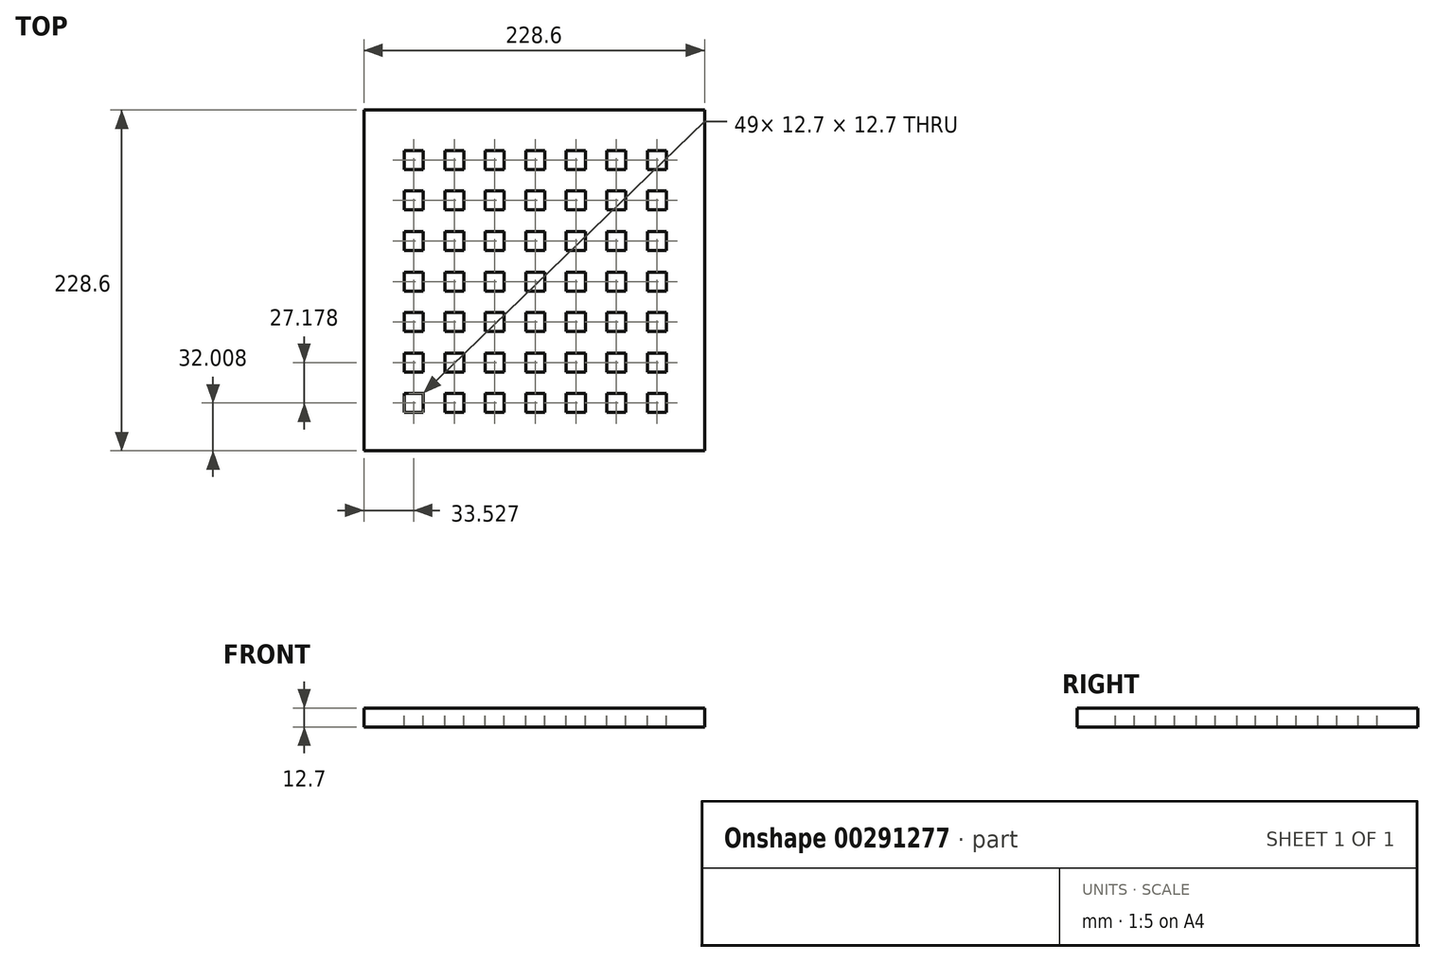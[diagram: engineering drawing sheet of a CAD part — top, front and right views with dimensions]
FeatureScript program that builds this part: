
annotation { "Feature Type Name" : "Feature", "Feature Type Description" : "" }
export const myFeature = defineFeature(function(context is Context, id is Id, definition is map)
    precondition{}
    {
        {
            var Q0;
            Q0=qCreatedBy(makeId("Top.planeOp"),FACE);
            var sketch = newSketch(context, id + "F0", { "sketchPlane" : qUnion([Q0])});
            skLineSegment(sketch, "E0.bottom", {"start": v(-111.6, 116.61) * mm, "end": v(117, 116.61) * mm});
            skLineSegment(sketch, "E0.top", {"start": v(-111.6, -111.99) * mm, "end": v(117, -111.99) * mm});
            skLineSegment(sketch, "E0.left", {"start": v(-111.6, 116.61) * mm, "end": v(-111.6, -111.99) * mm});
            skLineSegment(sketch, "E0.right", {"start": v(117, 116.61) * mm, "end": v(117, -111.99) * mm});
            skSolve(sketch);
        }
        {
            var Q0;
            Q0=makeQuery(id+"F0.imprint","IMPRINT",FACE,{"disambiguationData":[TD([[makeQuery(id+"F0.imprint","IMPRINT",EDGE,{"derivedFrom":sQuery(id+"F0.wireOp",EDGE,"E0.bottom")}),-1.0]])]});
            extrude(context, id + "F1", {"entities" : qUnion([Q0]), "depth" : 12.7 * mm});
        }
        {
            var Q0;
            Q0=makeQuery(id+"F1.opExtrude","CAP_FACE",FACE,{"disambiguationData":[OSD([sQuery(id+"F0.wireOp",EDGE,"E0.bottom"),sQuery(id+"F0.wireOp",EDGE,"E0.top"),sQuery(id+"F0.wireOp",EDGE,"E0.left"),sQuery(id+"F0.wireOp",EDGE,"E0.right")])],"isStart":false});
            var sketch = newSketch(context, id + "F2", { "sketchPlane" : qUnion([Q0])});
            skLineSegment(sketch, "E1.bottom", {"start": v(-111.6, 116.61) * mm, "end": v(-98.9, 116.61) * mm});
            skLineSegment(sketch, "E1.top", {"start": v(-111.6, 103.91) * mm, "end": v(-98.9, 103.91) * mm});
            skLineSegment(sketch, "E1.left", {"start": v(-111.6, 116.61) * mm, "end": v(-111.6, 103.91) * mm});
            skLineSegment(sketch, "E1.right", {"start": v(-98.9, 116.61) * mm, "end": v(-98.9, 103.91) * mm});
            skLineSegment(sketch, "E2.0.1.0", {"start": v(-98.9, 89.44) * mm, "end": v(-98.9, 76.74) * mm});
            skLineSegment(sketch, "E2.0.1.1", {"start": v(-111.6, 89.44) * mm, "end": v(-111.6, 76.74) * mm});
            skLineSegment(sketch, "E2.0.1.2", {"start": v(-111.6, 76.74) * mm, "end": v(-98.9, 76.74) * mm});
            skLineSegment(sketch, "E2.0.1.3", {"start": v(-111.6, 89.44) * mm, "end": v(-98.9, 89.44) * mm});
            skLineSegment(sketch, "E2.0.2.0", {"start": v(-98.9, 62.26) * mm, "end": v(-98.9, 49.56) * mm});
            skLineSegment(sketch, "E2.0.2.1", {"start": v(-111.6, 62.26) * mm, "end": v(-111.6, 49.56) * mm});
            skLineSegment(sketch, "E2.0.2.2", {"start": v(-111.6, 49.56) * mm, "end": v(-98.9, 49.56) * mm});
            skLineSegment(sketch, "E2.0.2.3", {"start": v(-111.6, 62.26) * mm, "end": v(-98.9, 62.26) * mm});
            skLineSegment(sketch, "E2.0.3.0", {"start": v(-98.9, 35.08) * mm, "end": v(-98.9, 22.38) * mm});
            skLineSegment(sketch, "E2.0.3.1", {"start": v(-111.6, 35.08) * mm, "end": v(-111.6, 22.38) * mm});
            skLineSegment(sketch, "E2.0.3.2", {"start": v(-111.6, 22.38) * mm, "end": v(-98.9, 22.38) * mm});
            skLineSegment(sketch, "E2.0.3.3", {"start": v(-111.6, 35.08) * mm, "end": v(-98.9, 35.08) * mm});
            skLineSegment(sketch, "E2.0.4.0", {"start": v(-98.9, 7.9) * mm, "end": v(-98.9, -4.8) * mm});
            skLineSegment(sketch, "E2.0.4.1", {"start": v(-111.6, 7.9) * mm, "end": v(-111.6, -4.8) * mm});
            skLineSegment(sketch, "E2.0.4.2", {"start": v(-111.6, -4.8) * mm, "end": v(-98.9, -4.8) * mm});
            skLineSegment(sketch, "E2.0.4.3", {"start": v(-111.6, 7.9) * mm, "end": v(-98.9, 7.9) * mm});
            skLineSegment(sketch, "E2.0.5.0", {"start": v(-98.9, -19.28) * mm, "end": v(-98.9, -31.98) * mm});
            skLineSegment(sketch, "E2.0.5.1", {"start": v(-111.6, -19.28) * mm, "end": v(-111.6, -31.98) * mm});
            skLineSegment(sketch, "E2.0.5.2", {"start": v(-111.6, -31.98) * mm, "end": v(-98.9, -31.98) * mm});
            skLineSegment(sketch, "E2.0.5.3", {"start": v(-111.6, -19.28) * mm, "end": v(-98.9, -19.28) * mm});
            skLineSegment(sketch, "E2.0.6.0", {"start": v(-98.9, -46.45) * mm, "end": v(-98.9, -59.15) * mm});
            skLineSegment(sketch, "E2.0.6.1", {"start": v(-111.6, -46.45) * mm, "end": v(-111.6, -59.15) * mm});
            skLineSegment(sketch, "E2.0.6.2", {"start": v(-111.6, -59.15) * mm, "end": v(-98.9, -59.15) * mm});
            skLineSegment(sketch, "E2.0.6.3", {"start": v(-111.6, -46.45) * mm, "end": v(-98.9, -46.45) * mm});
            skLineSegment(sketch, "E2.0.7.0", {"start": v(-98.9, -73.63) * mm, "end": v(-98.9, -86.33) * mm});
            skLineSegment(sketch, "E2.0.7.1", {"start": v(-111.6, -73.63) * mm, "end": v(-111.6, -86.33) * mm});
            skLineSegment(sketch, "E2.0.7.2", {"start": v(-111.6, -86.33) * mm, "end": v(-98.9, -86.33) * mm});
            skLineSegment(sketch, "E2.0.7.3", {"start": v(-111.6, -73.63) * mm, "end": v(-98.9, -73.63) * mm});
            skLineSegment(sketch, "E2.1.0.0", {"start": v(-71.71, 116.61) * mm, "end": v(-71.71, 103.91) * mm});
            skLineSegment(sketch, "E2.1.0.1", {"start": v(-84.41, 116.61) * mm, "end": v(-84.41, 103.91) * mm});
            skLineSegment(sketch, "E2.1.0.2", {"start": v(-84.41, 103.91) * mm, "end": v(-71.71, 103.91) * mm});
            skLineSegment(sketch, "E2.1.0.3", {"start": v(-84.41, 116.61) * mm, "end": v(-71.71, 116.61) * mm});
            skLineSegment(sketch, "E2.1.1.0", {"start": v(-71.71, 89.44) * mm, "end": v(-71.71, 76.74) * mm});
            skLineSegment(sketch, "E2.1.1.1", {"start": v(-84.41, 89.44) * mm, "end": v(-84.41, 76.74) * mm});
            skLineSegment(sketch, "E2.1.1.2", {"start": v(-84.41, 76.74) * mm, "end": v(-71.71, 76.74) * mm});
            skLineSegment(sketch, "E2.1.1.3", {"start": v(-84.41, 89.44) * mm, "end": v(-71.71, 89.44) * mm});
            skLineSegment(sketch, "E2.1.2.0", {"start": v(-71.71, 62.26) * mm, "end": v(-71.71, 49.56) * mm});
            skLineSegment(sketch, "E2.1.2.1", {"start": v(-84.41, 62.26) * mm, "end": v(-84.41, 49.56) * mm});
            skLineSegment(sketch, "E2.1.2.2", {"start": v(-84.41, 49.56) * mm, "end": v(-71.71, 49.56) * mm});
            skLineSegment(sketch, "E2.1.2.3", {"start": v(-84.41, 62.26) * mm, "end": v(-71.71, 62.26) * mm});
            skLineSegment(sketch, "E2.1.3.0", {"start": v(-71.71, 35.08) * mm, "end": v(-71.71, 22.38) * mm});
            skLineSegment(sketch, "E2.1.3.1", {"start": v(-84.41, 35.08) * mm, "end": v(-84.41, 22.38) * mm});
            skLineSegment(sketch, "E2.1.3.2", {"start": v(-84.41, 22.38) * mm, "end": v(-71.71, 22.38) * mm});
            skLineSegment(sketch, "E2.1.3.3", {"start": v(-84.41, 35.08) * mm, "end": v(-71.71, 35.08) * mm});
            skLineSegment(sketch, "E2.1.4.0", {"start": v(-71.71, 7.9) * mm, "end": v(-71.71, -4.8) * mm});
            skLineSegment(sketch, "E2.1.4.1", {"start": v(-84.41, 7.9) * mm, "end": v(-84.41, -4.8) * mm});
            skLineSegment(sketch, "E2.1.4.2", {"start": v(-84.41, -4.8) * mm, "end": v(-71.71, -4.8) * mm});
            skLineSegment(sketch, "E2.1.4.3", {"start": v(-84.41, 7.9) * mm, "end": v(-71.71, 7.9) * mm});
            skLineSegment(sketch, "E2.1.5.0", {"start": v(-71.71, -19.28) * mm, "end": v(-71.71, -31.98) * mm});
            skLineSegment(sketch, "E2.1.5.1", {"start": v(-84.41, -19.28) * mm, "end": v(-84.41, -31.98) * mm});
            skLineSegment(sketch, "E2.1.5.2", {"start": v(-84.41, -31.98) * mm, "end": v(-71.71, -31.98) * mm});
            skLineSegment(sketch, "E2.1.5.3", {"start": v(-84.41, -19.28) * mm, "end": v(-71.71, -19.28) * mm});
            skLineSegment(sketch, "E2.1.6.0", {"start": v(-71.71, -46.45) * mm, "end": v(-71.71, -59.15) * mm});
            skLineSegment(sketch, "E2.1.6.1", {"start": v(-84.41, -46.45) * mm, "end": v(-84.41, -59.15) * mm});
            skLineSegment(sketch, "E2.1.6.2", {"start": v(-84.41, -59.15) * mm, "end": v(-71.71, -59.15) * mm});
            skLineSegment(sketch, "E2.1.6.3", {"start": v(-84.41, -46.45) * mm, "end": v(-71.71, -46.45) * mm});
            skLineSegment(sketch, "E2.1.7.0", {"start": v(-71.71, -73.63) * mm, "end": v(-71.71, -86.33) * mm});
            skLineSegment(sketch, "E2.1.7.1", {"start": v(-84.41, -73.63) * mm, "end": v(-84.41, -86.33) * mm});
            skLineSegment(sketch, "E2.1.7.2", {"start": v(-84.41, -86.33) * mm, "end": v(-71.71, -86.33) * mm});
            skLineSegment(sketch, "E2.1.7.3", {"start": v(-84.41, -73.63) * mm, "end": v(-71.71, -73.63) * mm});
            skLineSegment(sketch, "E2.2.0.0", {"start": v(-44.53, 116.61) * mm, "end": v(-44.53, 103.91) * mm});
            skLineSegment(sketch, "E2.2.0.1", {"start": v(-57.23, 116.61) * mm, "end": v(-57.23, 103.91) * mm});
            skLineSegment(sketch, "E2.2.0.2", {"start": v(-57.23, 103.91) * mm, "end": v(-44.53, 103.91) * mm});
            skLineSegment(sketch, "E2.2.0.3", {"start": v(-57.23, 116.61) * mm, "end": v(-44.53, 116.61) * mm});
            skLineSegment(sketch, "E2.2.1.0", {"start": v(-44.53, 89.44) * mm, "end": v(-44.53, 76.74) * mm});
            skLineSegment(sketch, "E2.2.1.1", {"start": v(-57.23, 89.44) * mm, "end": v(-57.23, 76.74) * mm});
            skLineSegment(sketch, "E2.2.1.2", {"start": v(-57.23, 76.74) * mm, "end": v(-44.53, 76.74) * mm});
            skLineSegment(sketch, "E2.2.1.3", {"start": v(-57.23, 89.44) * mm, "end": v(-44.53, 89.44) * mm});
            skLineSegment(sketch, "E2.2.2.0", {"start": v(-44.53, 62.26) * mm, "end": v(-44.53, 49.56) * mm});
            skLineSegment(sketch, "E2.2.2.1", {"start": v(-57.23, 62.26) * mm, "end": v(-57.23, 49.56) * mm});
            skLineSegment(sketch, "E2.2.2.2", {"start": v(-57.23, 49.56) * mm, "end": v(-44.53, 49.56) * mm});
            skLineSegment(sketch, "E2.2.2.3", {"start": v(-57.23, 62.26) * mm, "end": v(-44.53, 62.26) * mm});
            skLineSegment(sketch, "E2.2.3.0", {"start": v(-44.53, 35.08) * mm, "end": v(-44.53, 22.38) * mm});
            skLineSegment(sketch, "E2.2.3.1", {"start": v(-57.23, 35.08) * mm, "end": v(-57.23, 22.38) * mm});
            skLineSegment(sketch, "E2.2.3.2", {"start": v(-57.23, 22.38) * mm, "end": v(-44.53, 22.38) * mm});
            skLineSegment(sketch, "E2.2.3.3", {"start": v(-57.23, 35.08) * mm, "end": v(-44.53, 35.08) * mm});
            skLineSegment(sketch, "E2.2.4.0", {"start": v(-44.53, 7.9) * mm, "end": v(-44.53, -4.8) * mm});
            skLineSegment(sketch, "E2.2.4.1", {"start": v(-57.23, 7.9) * mm, "end": v(-57.23, -4.8) * mm});
            skLineSegment(sketch, "E2.2.4.2", {"start": v(-57.23, -4.8) * mm, "end": v(-44.53, -4.8) * mm});
            skLineSegment(sketch, "E2.2.4.3", {"start": v(-57.23, 7.9) * mm, "end": v(-44.53, 7.9) * mm});
            skLineSegment(sketch, "E2.2.5.0", {"start": v(-44.53, -19.28) * mm, "end": v(-44.53, -31.98) * mm});
            skLineSegment(sketch, "E2.2.5.1", {"start": v(-57.23, -19.28) * mm, "end": v(-57.23, -31.98) * mm});
            skLineSegment(sketch, "E2.2.5.2", {"start": v(-57.23, -31.98) * mm, "end": v(-44.53, -31.98) * mm});
            skLineSegment(sketch, "E2.2.5.3", {"start": v(-57.23, -19.28) * mm, "end": v(-44.53, -19.28) * mm});
            skLineSegment(sketch, "E2.2.6.0", {"start": v(-44.53, -46.45) * mm, "end": v(-44.53, -59.15) * mm});
            skLineSegment(sketch, "E2.2.6.1", {"start": v(-57.23, -46.45) * mm, "end": v(-57.23, -59.15) * mm});
            skLineSegment(sketch, "E2.2.6.2", {"start": v(-57.23, -59.15) * mm, "end": v(-44.53, -59.15) * mm});
            skLineSegment(sketch, "E2.2.6.3", {"start": v(-57.23, -46.45) * mm, "end": v(-44.53, -46.45) * mm});
            skLineSegment(sketch, "E2.2.7.0", {"start": v(-44.53, -73.63) * mm, "end": v(-44.53, -86.33) * mm});
            skLineSegment(sketch, "E2.2.7.1", {"start": v(-57.23, -73.63) * mm, "end": v(-57.23, -86.33) * mm});
            skLineSegment(sketch, "E2.2.7.2", {"start": v(-57.23, -86.33) * mm, "end": v(-44.53, -86.33) * mm});
            skLineSegment(sketch, "E2.2.7.3", {"start": v(-57.23, -73.63) * mm, "end": v(-44.53, -73.63) * mm});
            skLineSegment(sketch, "E2.3.0.0", {"start": v(-17.36, 116.61) * mm, "end": v(-17.36, 103.91) * mm});
            skLineSegment(sketch, "E2.3.0.1", {"start": v(-30.06, 116.61) * mm, "end": v(-30.06, 103.91) * mm});
            skLineSegment(sketch, "E2.3.0.2", {"start": v(-30.06, 103.91) * mm, "end": v(-17.36, 103.91) * mm});
            skLineSegment(sketch, "E2.3.0.3", {"start": v(-30.06, 116.61) * mm, "end": v(-17.36, 116.61) * mm});
            skLineSegment(sketch, "E2.3.1.0", {"start": v(-17.36, 89.44) * mm, "end": v(-17.36, 76.74) * mm});
            skLineSegment(sketch, "E2.3.1.1", {"start": v(-30.06, 89.44) * mm, "end": v(-30.06, 76.74) * mm});
            skLineSegment(sketch, "E2.3.1.2", {"start": v(-30.06, 76.74) * mm, "end": v(-17.36, 76.74) * mm});
            skLineSegment(sketch, "E2.3.1.3", {"start": v(-30.06, 89.44) * mm, "end": v(-17.36, 89.44) * mm});
            skLineSegment(sketch, "E2.3.2.0", {"start": v(-17.36, 62.26) * mm, "end": v(-17.36, 49.56) * mm});
            skLineSegment(sketch, "E2.3.2.1", {"start": v(-30.06, 62.26) * mm, "end": v(-30.06, 49.56) * mm});
            skLineSegment(sketch, "E2.3.2.2", {"start": v(-30.06, 49.56) * mm, "end": v(-17.36, 49.56) * mm});
            skLineSegment(sketch, "E2.3.2.3", {"start": v(-30.06, 62.26) * mm, "end": v(-17.36, 62.26) * mm});
            skLineSegment(sketch, "E2.3.3.0", {"start": v(-17.36, 35.08) * mm, "end": v(-17.36, 22.38) * mm});
            skLineSegment(sketch, "E2.3.3.1", {"start": v(-30.06, 35.08) * mm, "end": v(-30.06, 22.38) * mm});
            skLineSegment(sketch, "E2.3.3.2", {"start": v(-30.06, 22.38) * mm, "end": v(-17.36, 22.38) * mm});
            skLineSegment(sketch, "E2.3.3.3", {"start": v(-30.06, 35.08) * mm, "end": v(-17.36, 35.08) * mm});
            skLineSegment(sketch, "E2.3.4.0", {"start": v(-17.36, 7.9) * mm, "end": v(-17.36, -4.8) * mm});
            skLineSegment(sketch, "E2.3.4.1", {"start": v(-30.06, 7.9) * mm, "end": v(-30.06, -4.8) * mm});
            skLineSegment(sketch, "E2.3.4.2", {"start": v(-30.06, -4.8) * mm, "end": v(-17.36, -4.8) * mm});
            skLineSegment(sketch, "E2.3.4.3", {"start": v(-30.06, 7.9) * mm, "end": v(-17.36, 7.9) * mm});
            skLineSegment(sketch, "E2.3.5.0", {"start": v(-17.36, -19.28) * mm, "end": v(-17.36, -31.98) * mm});
            skLineSegment(sketch, "E2.3.5.1", {"start": v(-30.06, -19.28) * mm, "end": v(-30.06, -31.98) * mm});
            skLineSegment(sketch, "E2.3.5.2", {"start": v(-30.06, -31.98) * mm, "end": v(-17.36, -31.98) * mm});
            skLineSegment(sketch, "E2.3.5.3", {"start": v(-30.06, -19.28) * mm, "end": v(-17.36, -19.28) * mm});
            skLineSegment(sketch, "E2.3.6.0", {"start": v(-17.36, -46.45) * mm, "end": v(-17.36, -59.15) * mm});
            skLineSegment(sketch, "E2.3.6.1", {"start": v(-30.06, -46.45) * mm, "end": v(-30.06, -59.15) * mm});
            skLineSegment(sketch, "E2.3.6.2", {"start": v(-30.06, -59.15) * mm, "end": v(-17.36, -59.15) * mm});
            skLineSegment(sketch, "E2.3.6.3", {"start": v(-30.06, -46.45) * mm, "end": v(-17.36, -46.45) * mm});
            skLineSegment(sketch, "E2.3.7.0", {"start": v(-17.36, -73.63) * mm, "end": v(-17.36, -86.33) * mm});
            skLineSegment(sketch, "E2.3.7.1", {"start": v(-30.06, -73.63) * mm, "end": v(-30.06, -86.33) * mm});
            skLineSegment(sketch, "E2.3.7.2", {"start": v(-30.06, -86.33) * mm, "end": v(-17.36, -86.33) * mm});
            skLineSegment(sketch, "E2.3.7.3", {"start": v(-30.06, -73.63) * mm, "end": v(-17.36, -73.63) * mm});
            skLineSegment(sketch, "E2.4.0.0", {"start": v(9.82, 116.61) * mm, "end": v(9.82, 103.91) * mm});
            skLineSegment(sketch, "E2.4.0.1", {"start": v(-2.88, 116.61) * mm, "end": v(-2.88, 103.91) * mm});
            skLineSegment(sketch, "E2.4.0.2", {"start": v(-2.88, 103.91) * mm, "end": v(9.82, 103.91) * mm});
            skLineSegment(sketch, "E2.4.0.3", {"start": v(-2.88, 116.61) * mm, "end": v(9.82, 116.61) * mm});
            skLineSegment(sketch, "E2.4.1.0", {"start": v(9.82, 89.44) * mm, "end": v(9.82, 76.74) * mm});
            skLineSegment(sketch, "E2.4.1.1", {"start": v(-2.88, 89.44) * mm, "end": v(-2.88, 76.74) * mm});
            skLineSegment(sketch, "E2.4.1.2", {"start": v(-2.88, 76.74) * mm, "end": v(9.82, 76.74) * mm});
            skLineSegment(sketch, "E2.4.1.3", {"start": v(-2.88, 89.44) * mm, "end": v(9.82, 89.44) * mm});
            skLineSegment(sketch, "E2.4.2.0", {"start": v(9.82, 62.26) * mm, "end": v(9.82, 49.56) * mm});
            skLineSegment(sketch, "E2.4.2.1", {"start": v(-2.88, 62.26) * mm, "end": v(-2.88, 49.56) * mm});
            skLineSegment(sketch, "E2.4.2.2", {"start": v(-2.88, 49.56) * mm, "end": v(9.82, 49.56) * mm});
            skLineSegment(sketch, "E2.4.2.3", {"start": v(-2.88, 62.26) * mm, "end": v(9.82, 62.26) * mm});
            skLineSegment(sketch, "E2.4.3.0", {"start": v(9.82, 35.08) * mm, "end": v(9.82, 22.38) * mm});
            skLineSegment(sketch, "E2.4.3.1", {"start": v(-2.88, 35.08) * mm, "end": v(-2.88, 22.38) * mm});
            skLineSegment(sketch, "E2.4.3.2", {"start": v(-2.88, 22.38) * mm, "end": v(9.82, 22.38) * mm});
            skLineSegment(sketch, "E2.4.3.3", {"start": v(-2.88, 35.08) * mm, "end": v(9.82, 35.08) * mm});
            skLineSegment(sketch, "E2.4.4.0", {"start": v(9.82, 7.9) * mm, "end": v(9.82, -4.8) * mm});
            skLineSegment(sketch, "E2.4.4.1", {"start": v(-2.88, 7.9) * mm, "end": v(-2.88, -4.8) * mm});
            skLineSegment(sketch, "E2.4.4.2", {"start": v(-2.88, -4.8) * mm, "end": v(9.82, -4.8) * mm});
            skLineSegment(sketch, "E2.4.4.3", {"start": v(-2.88, 7.9) * mm, "end": v(9.82, 7.9) * mm});
            skLineSegment(sketch, "E2.4.5.0", {"start": v(9.82, -19.28) * mm, "end": v(9.82, -31.98) * mm});
            skLineSegment(sketch, "E2.4.5.1", {"start": v(-2.88, -19.28) * mm, "end": v(-2.88, -31.98) * mm});
            skLineSegment(sketch, "E2.4.5.2", {"start": v(-2.88, -31.98) * mm, "end": v(9.82, -31.98) * mm});
            skLineSegment(sketch, "E2.4.5.3", {"start": v(-2.88, -19.28) * mm, "end": v(9.82, -19.28) * mm});
            skLineSegment(sketch, "E2.4.6.0", {"start": v(9.82, -46.45) * mm, "end": v(9.82, -59.15) * mm});
            skLineSegment(sketch, "E2.4.6.1", {"start": v(-2.88, -46.45) * mm, "end": v(-2.88, -59.15) * mm});
            skLineSegment(sketch, "E2.4.6.2", {"start": v(-2.88, -59.15) * mm, "end": v(9.82, -59.15) * mm});
            skLineSegment(sketch, "E2.4.6.3", {"start": v(-2.88, -46.45) * mm, "end": v(9.82, -46.45) * mm});
            skLineSegment(sketch, "E2.4.7.0", {"start": v(9.82, -73.63) * mm, "end": v(9.82, -86.33) * mm});
            skLineSegment(sketch, "E2.4.7.1", {"start": v(-2.88, -73.63) * mm, "end": v(-2.88, -86.33) * mm});
            skLineSegment(sketch, "E2.4.7.2", {"start": v(-2.88, -86.33) * mm, "end": v(9.82, -86.33) * mm});
            skLineSegment(sketch, "E2.4.7.3", {"start": v(-2.88, -73.63) * mm, "end": v(9.82, -73.63) * mm});
            skLineSegment(sketch, "E2.5.0.0", {"start": v(37, 116.61) * mm, "end": v(37, 103.91) * mm});
            skLineSegment(sketch, "E2.5.0.1", {"start": v(24.3, 116.61) * mm, "end": v(24.3, 103.91) * mm});
            skLineSegment(sketch, "E2.5.0.2", {"start": v(24.3, 103.91) * mm, "end": v(37, 103.91) * mm});
            skLineSegment(sketch, "E2.5.0.3", {"start": v(24.3, 116.61) * mm, "end": v(37, 116.61) * mm});
            skLineSegment(sketch, "E2.5.1.0", {"start": v(37, 89.44) * mm, "end": v(37, 76.74) * mm});
            skLineSegment(sketch, "E2.5.1.1", {"start": v(24.3, 89.44) * mm, "end": v(24.3, 76.74) * mm});
            skLineSegment(sketch, "E2.5.1.2", {"start": v(24.3, 76.74) * mm, "end": v(37, 76.74) * mm});
            skLineSegment(sketch, "E2.5.1.3", {"start": v(24.3, 89.44) * mm, "end": v(37, 89.44) * mm});
            skLineSegment(sketch, "E2.5.2.0", {"start": v(37, 62.26) * mm, "end": v(37, 49.56) * mm});
            skLineSegment(sketch, "E2.5.2.1", {"start": v(24.3, 62.26) * mm, "end": v(24.3, 49.56) * mm});
            skLineSegment(sketch, "E2.5.2.2", {"start": v(24.3, 49.56) * mm, "end": v(37, 49.56) * mm});
            skLineSegment(sketch, "E2.5.2.3", {"start": v(24.3, 62.26) * mm, "end": v(37, 62.26) * mm});
            skLineSegment(sketch, "E2.5.3.0", {"start": v(37, 35.08) * mm, "end": v(37, 22.38) * mm});
            skLineSegment(sketch, "E2.5.3.1", {"start": v(24.3, 35.08) * mm, "end": v(24.3, 22.38) * mm});
            skLineSegment(sketch, "E2.5.3.2", {"start": v(24.3, 22.38) * mm, "end": v(37, 22.38) * mm});
            skLineSegment(sketch, "E2.5.3.3", {"start": v(24.3, 35.08) * mm, "end": v(37, 35.08) * mm});
            skLineSegment(sketch, "E2.5.4.0", {"start": v(37, 7.9) * mm, "end": v(37, -4.8) * mm});
            skLineSegment(sketch, "E2.5.4.1", {"start": v(24.3, 7.9) * mm, "end": v(24.3, -4.8) * mm});
            skLineSegment(sketch, "E2.5.4.2", {"start": v(24.3, -4.8) * mm, "end": v(37, -4.8) * mm});
            skLineSegment(sketch, "E2.5.4.3", {"start": v(24.3, 7.9) * mm, "end": v(37, 7.9) * mm});
            skLineSegment(sketch, "E2.5.5.0", {"start": v(37, -19.28) * mm, "end": v(37, -31.98) * mm});
            skLineSegment(sketch, "E2.5.5.1", {"start": v(24.3, -19.28) * mm, "end": v(24.3, -31.98) * mm});
            skLineSegment(sketch, "E2.5.5.2", {"start": v(24.3, -31.98) * mm, "end": v(37, -31.98) * mm});
            skLineSegment(sketch, "E2.5.5.3", {"start": v(24.3, -19.28) * mm, "end": v(37, -19.28) * mm});
            skLineSegment(sketch, "E2.5.6.0", {"start": v(37, -46.45) * mm, "end": v(37, -59.15) * mm});
            skLineSegment(sketch, "E2.5.6.1", {"start": v(24.3, -46.45) * mm, "end": v(24.3, -59.15) * mm});
            skLineSegment(sketch, "E2.5.6.2", {"start": v(24.3, -59.15) * mm, "end": v(37, -59.15) * mm});
            skLineSegment(sketch, "E2.5.6.3", {"start": v(24.3, -46.45) * mm, "end": v(37, -46.45) * mm});
            skLineSegment(sketch, "E2.5.7.0", {"start": v(37, -73.63) * mm, "end": v(37, -86.33) * mm});
            skLineSegment(sketch, "E2.5.7.1", {"start": v(24.3, -73.63) * mm, "end": v(24.3, -86.33) * mm});
            skLineSegment(sketch, "E2.5.7.2", {"start": v(24.3, -86.33) * mm, "end": v(37, -86.33) * mm});
            skLineSegment(sketch, "E2.5.7.3", {"start": v(24.3, -73.63) * mm, "end": v(37, -73.63) * mm});
            skLineSegment(sketch, "E2.6.0.0", {"start": v(64.18, 116.61) * mm, "end": v(64.18, 103.91) * mm});
            skLineSegment(sketch, "E2.6.0.1", {"start": v(51.48, 116.61) * mm, "end": v(51.48, 103.91) * mm});
            skLineSegment(sketch, "E2.6.0.2", {"start": v(51.48, 103.91) * mm, "end": v(64.18, 103.91) * mm});
            skLineSegment(sketch, "E2.6.0.3", {"start": v(51.48, 116.61) * mm, "end": v(64.18, 116.61) * mm});
            skLineSegment(sketch, "E2.6.1.0", {"start": v(64.18, 89.44) * mm, "end": v(64.18, 76.74) * mm});
            skLineSegment(sketch, "E2.6.1.1", {"start": v(51.48, 89.44) * mm, "end": v(51.48, 76.74) * mm});
            skLineSegment(sketch, "E2.6.1.2", {"start": v(51.48, 76.74) * mm, "end": v(64.18, 76.74) * mm});
            skLineSegment(sketch, "E2.6.1.3", {"start": v(51.48, 89.44) * mm, "end": v(64.18, 89.44) * mm});
            skLineSegment(sketch, "E2.6.2.0", {"start": v(64.18, 62.26) * mm, "end": v(64.18, 49.56) * mm});
            skLineSegment(sketch, "E2.6.2.1", {"start": v(51.48, 62.26) * mm, "end": v(51.48, 49.56) * mm});
            skLineSegment(sketch, "E2.6.2.2", {"start": v(51.48, 49.56) * mm, "end": v(64.18, 49.56) * mm});
            skLineSegment(sketch, "E2.6.2.3", {"start": v(51.48, 62.26) * mm, "end": v(64.18, 62.26) * mm});
            skLineSegment(sketch, "E2.6.3.0", {"start": v(64.18, 35.08) * mm, "end": v(64.18, 22.38) * mm});
            skLineSegment(sketch, "E2.6.3.1", {"start": v(51.48, 35.08) * mm, "end": v(51.48, 22.38) * mm});
            skLineSegment(sketch, "E2.6.3.2", {"start": v(51.48, 22.38) * mm, "end": v(64.18, 22.38) * mm});
            skLineSegment(sketch, "E2.6.3.3", {"start": v(51.48, 35.08) * mm, "end": v(64.18, 35.08) * mm});
            skLineSegment(sketch, "E2.6.4.0", {"start": v(64.18, 7.9) * mm, "end": v(64.18, -4.8) * mm});
            skLineSegment(sketch, "E2.6.4.1", {"start": v(51.48, 7.9) * mm, "end": v(51.48, -4.8) * mm});
            skLineSegment(sketch, "E2.6.4.2", {"start": v(51.48, -4.8) * mm, "end": v(64.18, -4.8) * mm});
            skLineSegment(sketch, "E2.6.4.3", {"start": v(51.48, 7.9) * mm, "end": v(64.18, 7.9) * mm});
            skLineSegment(sketch, "E2.6.5.0", {"start": v(64.18, -19.28) * mm, "end": v(64.18, -31.98) * mm});
            skLineSegment(sketch, "E2.6.5.1", {"start": v(51.48, -19.28) * mm, "end": v(51.48, -31.98) * mm});
            skLineSegment(sketch, "E2.6.5.2", {"start": v(51.48, -31.98) * mm, "end": v(64.18, -31.98) * mm});
            skLineSegment(sketch, "E2.6.5.3", {"start": v(51.48, -19.28) * mm, "end": v(64.18, -19.28) * mm});
            skLineSegment(sketch, "E2.6.6.0", {"start": v(64.18, -46.45) * mm, "end": v(64.18, -59.15) * mm});
            skLineSegment(sketch, "E2.6.6.1", {"start": v(51.48, -46.45) * mm, "end": v(51.48, -59.15) * mm});
            skLineSegment(sketch, "E2.6.6.2", {"start": v(51.48, -59.15) * mm, "end": v(64.18, -59.15) * mm});
            skLineSegment(sketch, "E2.6.6.3", {"start": v(51.48, -46.45) * mm, "end": v(64.18, -46.45) * mm});
            skLineSegment(sketch, "E2.6.7.0", {"start": v(64.18, -73.63) * mm, "end": v(64.18, -86.33) * mm});
            skLineSegment(sketch, "E2.6.7.1", {"start": v(51.48, -73.63) * mm, "end": v(51.48, -86.33) * mm});
            skLineSegment(sketch, "E2.6.7.2", {"start": v(51.48, -86.33) * mm, "end": v(64.18, -86.33) * mm});
            skLineSegment(sketch, "E2.6.7.3", {"start": v(51.48, -73.63) * mm, "end": v(64.18, -73.63) * mm});
            skLineSegment(sketch, "E2.7.0.0", {"start": v(91.36, 116.61) * mm, "end": v(91.36, 103.91) * mm});
            skLineSegment(sketch, "E2.7.0.1", {"start": v(78.66, 116.61) * mm, "end": v(78.66, 103.91) * mm});
            skLineSegment(sketch, "E2.7.0.2", {"start": v(78.66, 103.91) * mm, "end": v(91.36, 103.91) * mm});
            skLineSegment(sketch, "E2.7.0.3", {"start": v(78.66, 116.61) * mm, "end": v(91.36, 116.61) * mm});
            skLineSegment(sketch, "E2.7.1.0", {"start": v(91.36, 89.44) * mm, "end": v(91.36, 76.74) * mm});
            skLineSegment(sketch, "E2.7.1.1", {"start": v(78.66, 89.44) * mm, "end": v(78.66, 76.74) * mm});
            skLineSegment(sketch, "E2.7.1.2", {"start": v(78.66, 76.74) * mm, "end": v(91.36, 76.74) * mm});
            skLineSegment(sketch, "E2.7.1.3", {"start": v(78.66, 89.44) * mm, "end": v(91.36, 89.44) * mm});
            skLineSegment(sketch, "E2.7.2.0", {"start": v(91.36, 62.26) * mm, "end": v(91.36, 49.56) * mm});
            skLineSegment(sketch, "E2.7.2.1", {"start": v(78.66, 62.26) * mm, "end": v(78.66, 49.56) * mm});
            skLineSegment(sketch, "E2.7.2.2", {"start": v(78.66, 49.56) * mm, "end": v(91.36, 49.56) * mm});
            skLineSegment(sketch, "E2.7.2.3", {"start": v(78.66, 62.26) * mm, "end": v(91.36, 62.26) * mm});
            skLineSegment(sketch, "E2.7.3.0", {"start": v(91.36, 35.08) * mm, "end": v(91.36, 22.38) * mm});
            skLineSegment(sketch, "E2.7.3.1", {"start": v(78.66, 35.08) * mm, "end": v(78.66, 22.38) * mm});
            skLineSegment(sketch, "E2.7.3.2", {"start": v(78.66, 22.38) * mm, "end": v(91.36, 22.38) * mm});
            skLineSegment(sketch, "E2.7.3.3", {"start": v(78.66, 35.08) * mm, "end": v(91.36, 35.08) * mm});
            skLineSegment(sketch, "E2.7.4.0", {"start": v(91.36, 7.9) * mm, "end": v(91.36, -4.8) * mm});
            skLineSegment(sketch, "E2.7.4.1", {"start": v(78.66, 7.9) * mm, "end": v(78.66, -4.8) * mm});
            skLineSegment(sketch, "E2.7.4.2", {"start": v(78.66, -4.8) * mm, "end": v(91.36, -4.8) * mm});
            skLineSegment(sketch, "E2.7.4.3", {"start": v(78.66, 7.9) * mm, "end": v(91.36, 7.9) * mm});
            skLineSegment(sketch, "E2.7.5.0", {"start": v(91.36, -19.28) * mm, "end": v(91.36, -31.98) * mm});
            skLineSegment(sketch, "E2.7.5.1", {"start": v(78.66, -19.28) * mm, "end": v(78.66, -31.98) * mm});
            skLineSegment(sketch, "E2.7.5.2", {"start": v(78.66, -31.98) * mm, "end": v(91.36, -31.98) * mm});
            skLineSegment(sketch, "E2.7.5.3", {"start": v(78.66, -19.28) * mm, "end": v(91.36, -19.28) * mm});
            skLineSegment(sketch, "E2.7.6.0", {"start": v(91.36, -46.45) * mm, "end": v(91.36, -59.15) * mm});
            skLineSegment(sketch, "E2.7.6.1", {"start": v(78.66, -46.45) * mm, "end": v(78.66, -59.15) * mm});
            skLineSegment(sketch, "E2.7.6.2", {"start": v(78.66, -59.15) * mm, "end": v(91.36, -59.15) * mm});
            skLineSegment(sketch, "E2.7.6.3", {"start": v(78.66, -46.45) * mm, "end": v(91.36, -46.45) * mm});
            skLineSegment(sketch, "E2.7.7.0", {"start": v(91.36, -73.63) * mm, "end": v(91.36, -86.33) * mm});
            skLineSegment(sketch, "E2.7.7.1", {"start": v(78.66, -73.63) * mm, "end": v(78.66, -86.33) * mm});
            skLineSegment(sketch, "E2.7.7.2", {"start": v(78.66, -86.33) * mm, "end": v(91.36, -86.33) * mm});
            skLineSegment(sketch, "E2.7.7.3", {"start": v(78.66, -73.63) * mm, "end": v(91.36, -73.63) * mm});
            skLineSegment(sketch, "E2.direction1", {"start": v(-111.6, 103.91) * mm, "end": v(-84.41, 103.91) * mm, "construction": true});
            skLineSegment(sketch, "E2.direction2", {"start": v(-111.6, 103.91) * mm, "end": v(-111.6, 76.74) * mm, "construction": true});
            skSolve(sketch);
        }
        {
            var Q0;
            Q0=makeQuery(id+"F2.imprint","IMPRINT",FACE,{"disambiguationData":[TD([[makeQuery(id+"F2.imprint","IMPRINT",EDGE,{"derivedFrom":sQuery(id+"F2.wireOp",EDGE,"E2.1.1.0")}),-1.0]])]});
            var Q1;
            Q1=makeQuery(id+"F2.imprint","IMPRINT",FACE,{"disambiguationData":[TD([[makeQuery(id+"F2.imprint","IMPRINT",EDGE,{"derivedFrom":sQuery(id+"F2.wireOp",EDGE,"E2.2.1.0")}),-1.0]])]});
            var Q2;
            Q2=makeQuery(id+"F2.imprint","IMPRINT",FACE,{"disambiguationData":[TD([[makeQuery(id+"F2.imprint","IMPRINT",EDGE,{"derivedFrom":sQuery(id+"F2.wireOp",EDGE,"E2.3.1.0")}),-1.0]])]});
            var Q3;
            Q3=makeQuery(id+"F2.imprint","IMPRINT",FACE,{"disambiguationData":[TD([[makeQuery(id+"F2.imprint","IMPRINT",EDGE,{"derivedFrom":sQuery(id+"F2.wireOp",EDGE,"E2.4.1.0")}),-1.0]])]});
            var Q4;
            Q4=makeQuery(id+"F2.imprint","IMPRINT",FACE,{"disambiguationData":[TD([[makeQuery(id+"F2.imprint","IMPRINT",EDGE,{"derivedFrom":sQuery(id+"F2.wireOp",EDGE,"E2.5.1.0")}),-1.0]])]});
            var Q5;
            Q5=makeQuery(id+"F2.imprint","IMPRINT",FACE,{"disambiguationData":[TD([[makeQuery(id+"F2.imprint","IMPRINT",EDGE,{"derivedFrom":sQuery(id+"F2.wireOp",EDGE,"E2.6.1.0")}),-1.0]])]});
            var Q6;
            Q6=makeQuery(id+"F2.imprint","IMPRINT",FACE,{"disambiguationData":[TD([[makeQuery(id+"F2.imprint","IMPRINT",EDGE,{"derivedFrom":sQuery(id+"F2.wireOp",EDGE,"E2.7.1.0")}),-1.0]])]});
            var Q7;
            Q7=makeQuery(id+"F2.imprint","IMPRINT",FACE,{"disambiguationData":[TD([[makeQuery(id+"F2.imprint","IMPRINT",EDGE,{"derivedFrom":sQuery(id+"F2.wireOp",EDGE,"E2.7.2.0")}),-1.0]])]});
            var Q8;
            Q8=makeQuery(id+"F2.imprint","IMPRINT",FACE,{"disambiguationData":[TD([[makeQuery(id+"F2.imprint","IMPRINT",EDGE,{"derivedFrom":sQuery(id+"F2.wireOp",EDGE,"E2.6.2.0")}),-1.0]])]});
            var Q9;
            Q9=makeQuery(id+"F2.imprint","IMPRINT",FACE,{"disambiguationData":[TD([[makeQuery(id+"F2.imprint","IMPRINT",EDGE,{"derivedFrom":sQuery(id+"F2.wireOp",EDGE,"E2.5.2.0")}),-1.0]])]});
            var Q10;
            Q10=makeQuery(id+"F2.imprint","IMPRINT",FACE,{"disambiguationData":[TD([[makeQuery(id+"F2.imprint","IMPRINT",EDGE,{"derivedFrom":sQuery(id+"F2.wireOp",EDGE,"E2.4.2.0")}),-1.0]])]});
            var Q11;
            Q11=makeQuery(id+"F2.imprint","IMPRINT",FACE,{"disambiguationData":[TD([[makeQuery(id+"F2.imprint","IMPRINT",EDGE,{"derivedFrom":sQuery(id+"F2.wireOp",EDGE,"E2.3.2.0")}),-1.0]])]});
            var Q12;
            Q12=makeQuery(id+"F2.imprint","IMPRINT",FACE,{"disambiguationData":[TD([[makeQuery(id+"F2.imprint","IMPRINT",EDGE,{"derivedFrom":sQuery(id+"F2.wireOp",EDGE,"E2.2.2.0")}),-1.0]])]});
            var Q13;
            Q13=makeQuery(id+"F2.imprint","IMPRINT",FACE,{"disambiguationData":[TD([[makeQuery(id+"F2.imprint","IMPRINT",EDGE,{"derivedFrom":sQuery(id+"F2.wireOp",EDGE,"E2.1.2.0")}),-1.0]])]});
            var Q14;
            Q14=makeQuery(id+"F2.imprint","IMPRINT",FACE,{"disambiguationData":[TD([[makeQuery(id+"F2.imprint","IMPRINT",EDGE,{"derivedFrom":sQuery(id+"F2.wireOp",EDGE,"E2.1.3.0")}),-1.0]])]});
            var Q15;
            Q15=makeQuery(id+"F2.imprint","IMPRINT",FACE,{"disambiguationData":[TD([[makeQuery(id+"F2.imprint","IMPRINT",EDGE,{"derivedFrom":sQuery(id+"F2.wireOp",EDGE,"E2.2.3.0")}),-1.0]])]});
            var Q16;
            Q16=makeQuery(id+"F2.imprint","IMPRINT",FACE,{"disambiguationData":[TD([[makeQuery(id+"F2.imprint","IMPRINT",EDGE,{"derivedFrom":sQuery(id+"F2.wireOp",EDGE,"E2.3.3.0")}),-1.0]])]});
            var Q17;
            Q17=makeQuery(id+"F2.imprint","IMPRINT",FACE,{"disambiguationData":[TD([[makeQuery(id+"F2.imprint","IMPRINT",EDGE,{"derivedFrom":sQuery(id+"F2.wireOp",EDGE,"E2.4.3.0")}),-1.0]])]});
            var Q18;
            Q18=makeQuery(id+"F2.imprint","IMPRINT",FACE,{"disambiguationData":[TD([[makeQuery(id+"F2.imprint","IMPRINT",EDGE,{"derivedFrom":sQuery(id+"F2.wireOp",EDGE,"E2.5.3.0")}),-1.0]])]});
            var Q19;
            Q19=makeQuery(id+"F2.imprint","IMPRINT",FACE,{"disambiguationData":[TD([[makeQuery(id+"F2.imprint","IMPRINT",EDGE,{"derivedFrom":sQuery(id+"F2.wireOp",EDGE,"E2.6.3.0")}),-1.0]])]});
            var Q20;
            Q20=makeQuery(id+"F2.imprint","IMPRINT",FACE,{"disambiguationData":[TD([[makeQuery(id+"F2.imprint","IMPRINT",EDGE,{"derivedFrom":sQuery(id+"F2.wireOp",EDGE,"E2.7.3.0")}),-1.0]])]});
            var Q21;
            Q21=makeQuery(id+"F2.imprint","IMPRINT",FACE,{"disambiguationData":[TD([[makeQuery(id+"F2.imprint","IMPRINT",EDGE,{"derivedFrom":sQuery(id+"F2.wireOp",EDGE,"E2.6.4.0")}),-1.0]])]});
            var Q22;
            Q22=makeQuery(id+"F2.imprint","IMPRINT",FACE,{"disambiguationData":[TD([[makeQuery(id+"F2.imprint","IMPRINT",EDGE,{"derivedFrom":sQuery(id+"F2.wireOp",EDGE,"E2.5.4.0")}),-1.0]])]});
            var Q23;
            Q23=makeQuery(id+"F2.imprint","IMPRINT",FACE,{"disambiguationData":[TD([[makeQuery(id+"F2.imprint","IMPRINT",EDGE,{"derivedFrom":sQuery(id+"F2.wireOp",EDGE,"E2.7.4.0")}),-1.0]])]});
            var Q24;
            Q24=makeQuery(id+"F2.imprint","IMPRINT",FACE,{"disambiguationData":[TD([[makeQuery(id+"F2.imprint","IMPRINT",EDGE,{"derivedFrom":sQuery(id+"F2.wireOp",EDGE,"E2.4.4.0")}),-1.0]])]});
            var Q25;
            Q25=makeQuery(id+"F2.imprint","IMPRINT",FACE,{"disambiguationData":[TD([[makeQuery(id+"F2.imprint","IMPRINT",EDGE,{"derivedFrom":sQuery(id+"F2.wireOp",EDGE,"E2.3.4.0")}),-1.0]])]});
            var Q26;
            Q26=makeQuery(id+"F2.imprint","IMPRINT",FACE,{"disambiguationData":[TD([[makeQuery(id+"F2.imprint","IMPRINT",EDGE,{"derivedFrom":sQuery(id+"F2.wireOp",EDGE,"E2.2.4.0")}),-1.0]])]});
            var Q27;
            Q27=makeQuery(id+"F2.imprint","IMPRINT",FACE,{"disambiguationData":[TD([[makeQuery(id+"F2.imprint","IMPRINT",EDGE,{"derivedFrom":sQuery(id+"F2.wireOp",EDGE,"E2.1.4.0")}),-1.0]])]});
            var Q28;
            Q28=makeQuery(id+"F2.imprint","IMPRINT",FACE,{"disambiguationData":[TD([[makeQuery(id+"F2.imprint","IMPRINT",EDGE,{"derivedFrom":sQuery(id+"F2.wireOp",EDGE,"E2.1.5.0")}),-1.0]])]});
            var Q29;
            Q29=makeQuery(id+"F2.imprint","IMPRINT",FACE,{"disambiguationData":[TD([[makeQuery(id+"F2.imprint","IMPRINT",EDGE,{"derivedFrom":sQuery(id+"F2.wireOp",EDGE,"E2.1.6.0")}),-1.0]])]});
            var Q30;
            Q30=makeQuery(id+"F2.imprint","IMPRINT",FACE,{"disambiguationData":[TD([[makeQuery(id+"F2.imprint","IMPRINT",EDGE,{"derivedFrom":sQuery(id+"F2.wireOp",EDGE,"E2.1.7.0")}),-1.0]])]});
            var Q31;
            Q31=makeQuery(id+"F2.imprint","IMPRINT",FACE,{"disambiguationData":[TD([[makeQuery(id+"F2.imprint","IMPRINT",EDGE,{"derivedFrom":sQuery(id+"F2.wireOp",EDGE,"E2.2.7.0")}),-1.0]])]});
            var Q32;
            Q32=makeQuery(id+"F2.imprint","IMPRINT",FACE,{"disambiguationData":[TD([[makeQuery(id+"F2.imprint","IMPRINT",EDGE,{"derivedFrom":sQuery(id+"F2.wireOp",EDGE,"E2.2.6.0")}),-1.0]])]});
            var Q33;
            Q33=makeQuery(id+"F2.imprint","IMPRINT",FACE,{"disambiguationData":[TD([[makeQuery(id+"F2.imprint","IMPRINT",EDGE,{"derivedFrom":sQuery(id+"F2.wireOp",EDGE,"E2.2.5.0")}),-1.0]])]});
            var Q34;
            Q34=makeQuery(id+"F2.imprint","IMPRINT",FACE,{"disambiguationData":[TD([[makeQuery(id+"F2.imprint","IMPRINT",EDGE,{"derivedFrom":sQuery(id+"F2.wireOp",EDGE,"E2.3.5.0")}),-1.0]])]});
            var Q35;
            Q35=makeQuery(id+"F2.imprint","IMPRINT",FACE,{"disambiguationData":[TD([[makeQuery(id+"F2.imprint","IMPRINT",EDGE,{"derivedFrom":sQuery(id+"F2.wireOp",EDGE,"E2.3.6.0")}),-1.0]])]});
            var Q36;
            Q36=makeQuery(id+"F2.imprint","IMPRINT",FACE,{"disambiguationData":[TD([[makeQuery(id+"F2.imprint","IMPRINT",EDGE,{"derivedFrom":sQuery(id+"F2.wireOp",EDGE,"E2.3.7.0")}),-1.0]])]});
            var Q37;
            Q37=makeQuery(id+"F2.imprint","IMPRINT",FACE,{"disambiguationData":[TD([[makeQuery(id+"F2.imprint","IMPRINT",EDGE,{"derivedFrom":sQuery(id+"F2.wireOp",EDGE,"E2.4.7.0")}),-1.0]])]});
            var Q38;
            Q38=makeQuery(id+"F2.imprint","IMPRINT",FACE,{"disambiguationData":[TD([[makeQuery(id+"F2.imprint","IMPRINT",EDGE,{"derivedFrom":sQuery(id+"F2.wireOp",EDGE,"E2.4.6.0")}),-1.0]])]});
            var Q39;
            Q39=makeQuery(id+"F2.imprint","IMPRINT",FACE,{"disambiguationData":[TD([[makeQuery(id+"F2.imprint","IMPRINT",EDGE,{"derivedFrom":sQuery(id+"F2.wireOp",EDGE,"E2.4.5.0")}),-1.0]])]});
            var Q40;
            Q40=makeQuery(id+"F2.imprint","IMPRINT",FACE,{"disambiguationData":[TD([[makeQuery(id+"F2.imprint","IMPRINT",EDGE,{"derivedFrom":sQuery(id+"F2.wireOp",EDGE,"E2.5.5.0")}),-1.0]])]});
            var Q41;
            Q41=makeQuery(id+"F2.imprint","IMPRINT",FACE,{"disambiguationData":[TD([[makeQuery(id+"F2.imprint","IMPRINT",EDGE,{"derivedFrom":sQuery(id+"F2.wireOp",EDGE,"E2.5.6.0")}),-1.0]])]});
            var Q42;
            Q42=makeQuery(id+"F2.imprint","IMPRINT",FACE,{"disambiguationData":[TD([[makeQuery(id+"F2.imprint","IMPRINT",EDGE,{"derivedFrom":sQuery(id+"F2.wireOp",EDGE,"E2.5.7.0")}),-1.0]])]});
            var Q43;
            Q43=makeQuery(id+"F2.imprint","IMPRINT",FACE,{"disambiguationData":[TD([[makeQuery(id+"F2.imprint","IMPRINT",EDGE,{"derivedFrom":sQuery(id+"F2.wireOp",EDGE,"E2.6.7.0")}),-1.0]])]});
            var Q44;
            Q44=makeQuery(id+"F2.imprint","IMPRINT",FACE,{"disambiguationData":[TD([[makeQuery(id+"F2.imprint","IMPRINT",EDGE,{"derivedFrom":sQuery(id+"F2.wireOp",EDGE,"E2.6.6.0")}),-1.0]])]});
            var Q45;
            Q45=makeQuery(id+"F2.imprint","IMPRINT",FACE,{"disambiguationData":[TD([[makeQuery(id+"F2.imprint","IMPRINT",EDGE,{"derivedFrom":sQuery(id+"F2.wireOp",EDGE,"E2.6.5.0")}),-1.0]])]});
            var Q46;
            Q46=makeQuery(id+"F2.imprint","IMPRINT",FACE,{"disambiguationData":[TD([[makeQuery(id+"F2.imprint","IMPRINT",EDGE,{"derivedFrom":sQuery(id+"F2.wireOp",EDGE,"E2.7.5.0")}),-1.0]])]});
            var Q47;
            Q47=makeQuery(id+"F2.imprint","IMPRINT",FACE,{"disambiguationData":[TD([[makeQuery(id+"F2.imprint","IMPRINT",EDGE,{"derivedFrom":sQuery(id+"F2.wireOp",EDGE,"E2.7.6.0")}),-1.0]])]});
            var Q48;
            Q48=makeQuery(id+"F2.imprint","IMPRINT",FACE,{"disambiguationData":[TD([[makeQuery(id+"F2.imprint","IMPRINT",EDGE,{"derivedFrom":sQuery(id+"F2.wireOp",EDGE,"E2.7.7.0")}),-1.0]])]});
            extrude(context, id + "F3", {"entities" : qUnion([Q0, Q1, Q2, Q3, Q4, Q5, Q6, Q7, Q8, Q9, Q10, Q11, Q12, Q13, Q14, Q15, Q16, Q17, Q18, Q19, Q20, Q21, Q22, Q23, Q24, Q25, Q26, Q27, Q28, Q29, Q30, Q31, Q32, Q33, Q34, Q35, Q36, Q37, Q38, Q39, Q40, Q41, Q42, Q43, Q44, Q45, Q46, Q47, Q48]), "operationType" : NewBodyOperationType.REMOVE, "oppositeDirection" : true, "depth" : 25.4 * mm});
        }
    });
